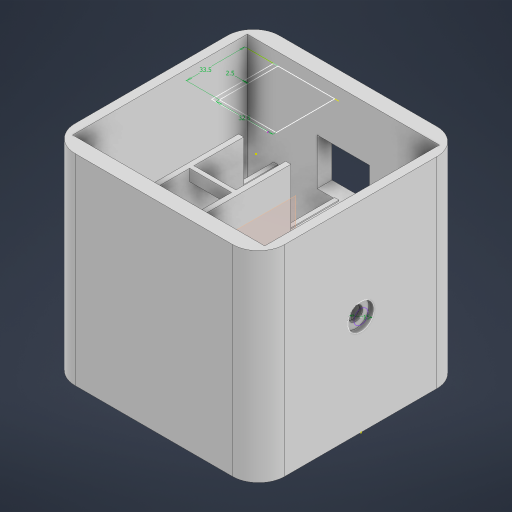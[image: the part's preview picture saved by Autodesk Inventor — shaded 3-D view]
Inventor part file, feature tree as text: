
AUTODESK INVENTOR PART (.ipt)
format: ipt  version: 2023 (Build 270158030, 158C)  size: 472,576 bytes
history: native  units: in
note: dims shown in document units (in); Inventor stores cm internally (conversion verified against a paired STEP export)
features: extrude x25, sketch x23, fillet x5, plane x2, loft x1
ambient origin geometry x8: Origin, YZ Plane, XZ Plane, XY Plane, X Axis, Y Axis, Z Axis, Center Point
bodies: Solid1 (feature_tree)
feature tree (56):
  extrude  "Extrusion1"  Depth=4.7244in
  sketch  "Sketch3"  dims[d2=2.3031in d3=2.3622in]
  extrude  "Extrusion3"  Depth=2.3622in
  loft  "Loft1"
  extrude  "Extrusion7"  Depth=2.2638in
  plane  "Work Plane2"
  extrude  "Extrusion8"  Depth=0.1969in
  plane  "Work Plane3"
  extrude  "Extrusion9"  Depth=0.3346in
  extrude  "Extrusion10"  Depth=1.1024in
  extrude  "Extrusion17"  Depth=1.5748in
  extrude  "Extrusion18"  Depth=1.5748in
  extrude  "Extrusion19"  Depth=1.1811in
  extrude  "Extrusion21"  TaperAngle=0.0deg  [1 undecoded]
  extrude  "Extrusion22"  Depth=1.1811in TaperAngle=0.0deg
  extrude  "Extrusion23"  Depth=2.5591in
  extrude  "Extrusion25"  TaperAngle=0.0deg  [1 undecoded]
  fillet  "Face Fillet1"
  sketch  "Sketch57"  dims[d119=1.1811in d120=2.2992in]
  extrude  "Extrusion26"  Depth=0.1181in
  extrude  "Extrusion27"  Depth=0.3346in TaperAngle=0.0deg
  sketch  "Sketch58"  dims[d121=0.0787in d123=1.1811in d124=0.0in]
  sketch  "Sketch59"  dims[d125=0.9055in d126=0.0787in]
  extrude  "Extrusion28"  Depth=2.2992in
  sketch  "Sketch60"  dims[d127=0.0984in d128=1.063in d129=0.0in]
  extrude  "Extrusion29"  Depth=1.1811in TaperAngle=0.0deg
  extrude  "Extrusion30"  Depth=0.0787in
  extrude  "Extrusion32"  Depth=1.063in TaperAngle=0.0deg
  extrude  "Extrusion33"  Depth=0.0394in TaperAngle=0.0deg
  extrude  "Extrusion34"  TaperAngle=0.0deg  [1 undecoded]
  extrude  "Extrusion35"  Depth=0.1969in
  extrude  "Extrusion36"  Depth=0.374in
  extrude  "Extrusion37"  TaperAngle=0.0deg  [1 undecoded]
  fillet  "Face Fillet2"
  fillet  "Face Fillet3"
  fillet  "Face Fillet4"
  fillet  "Face Fillet5"
  extrude  "Extrusion38"  Depth=1.7717in TaperAngle=0.0deg
  sketch  "Sketch2"  dims[d0=4.6063in d1=4.7244in]
  sketch  "Sketch4"  dims[d4=4.5276in d5=0.0in d6=0.315in]
  sketch  "Sketch13"  dims[d7=2.2638in d8=2.3031in]
  sketch  "Sketch14"  dims[d11=4.3307in d12=0.1969in]
  sketch  "Sketch18"  dims[d13=3.937in d14=0.3346in]
  sketch  "Sketch28"  dims[d15=4.3307in d16=0.0in d44=1.1024in]
  sketch  "Sketch31"  dims[d45=1.5748in d46=1.5748in]
  sketch  "Sketch32"  dims[d47=0.0in d48=1.5748in]
  sketch  "Sketch43"  dims[d49=1.5748in d50=1.1811in]
  sketch  "Sketch44"  dims[d51=0.0in d52=90.0deg d53=0.0in d54=90.0deg]
  sketch  "Sketch46"  dims[d57=1.7717in d58=1.1811in d59=0.0in]
  sketch  "Sketch49"  dims[d74=0.0in d75=2.5591in]
  sketch  "Sketch50"  dims[d76=0.1181in d77=0.0in d78=0.0in]
  sketch  "Sketch51"  dims[d79=0.1181in d80=0.0in d81=0.6063in]
  sketch  "Sketch54"  dims[d82=1.1811in d83=0.0in d117=0.3346in d118=0.0in]
  sketch  "Sketch62"  dims[d134=0.1378in d135=0.0in d136=0.0394in d137=0.0in]
  sketch  "Sketch63"  dims[d138=0.0in d139=0.0in]
  sketch  "Sketch65"  dims[d140=0.1181in d141=0.0in d148=0.1969in d150=0.374in d151=0.0in d152=1.7717in d153=0.0in d154=0.3937in d156=0.5906in d157=0.1969in d158=0.0in d159=0.1181in d160=0.0in d161=1.3976in d162=1.4764in d163=0.0in d164=1.4764in d165=1.3976in d166=0.0in d167=4.0551in d168=0.0in d169=1.2795in d170=0.0984in d171=1.3189in d172=4.0551in d173=0.0in d174=1.2795in d175=1.3189in d176=0.0984in d177=3.8976in d178=0.0in d181=3.8976in d182=0.0in d183=1.9291in d184=0.0in d185=1.2795in d186=0.1969in d187=0.3543in d188=0.0in d189=1.2795in d190=0.1969in d191=0.3543in d192=0.0in d193=0.5906in d194=0.1969in d195=0.0in d196=0.1181in d197=0.0in d198=0.5906in d199=0.5906in d200=0.5906in d201=0.5906in d202=1.9291in d203=0.0in d43=0.0in d87=0.0197in d88=0.0344in d89=0.0197in d90=0.0344in d144=0.0197in d145=0.0344in d146=0.0197in d147=0.0344in d179=0.0197in d180=0.0344in d204=0.0197in d205=0.0344in d206=0.0in d207=0.0in]
note: 4 required parameter values undecoded (feature->parameter linkage not recoverable at this tier; creation-order binding heuristic only, values carry confidence <= 0.55)
